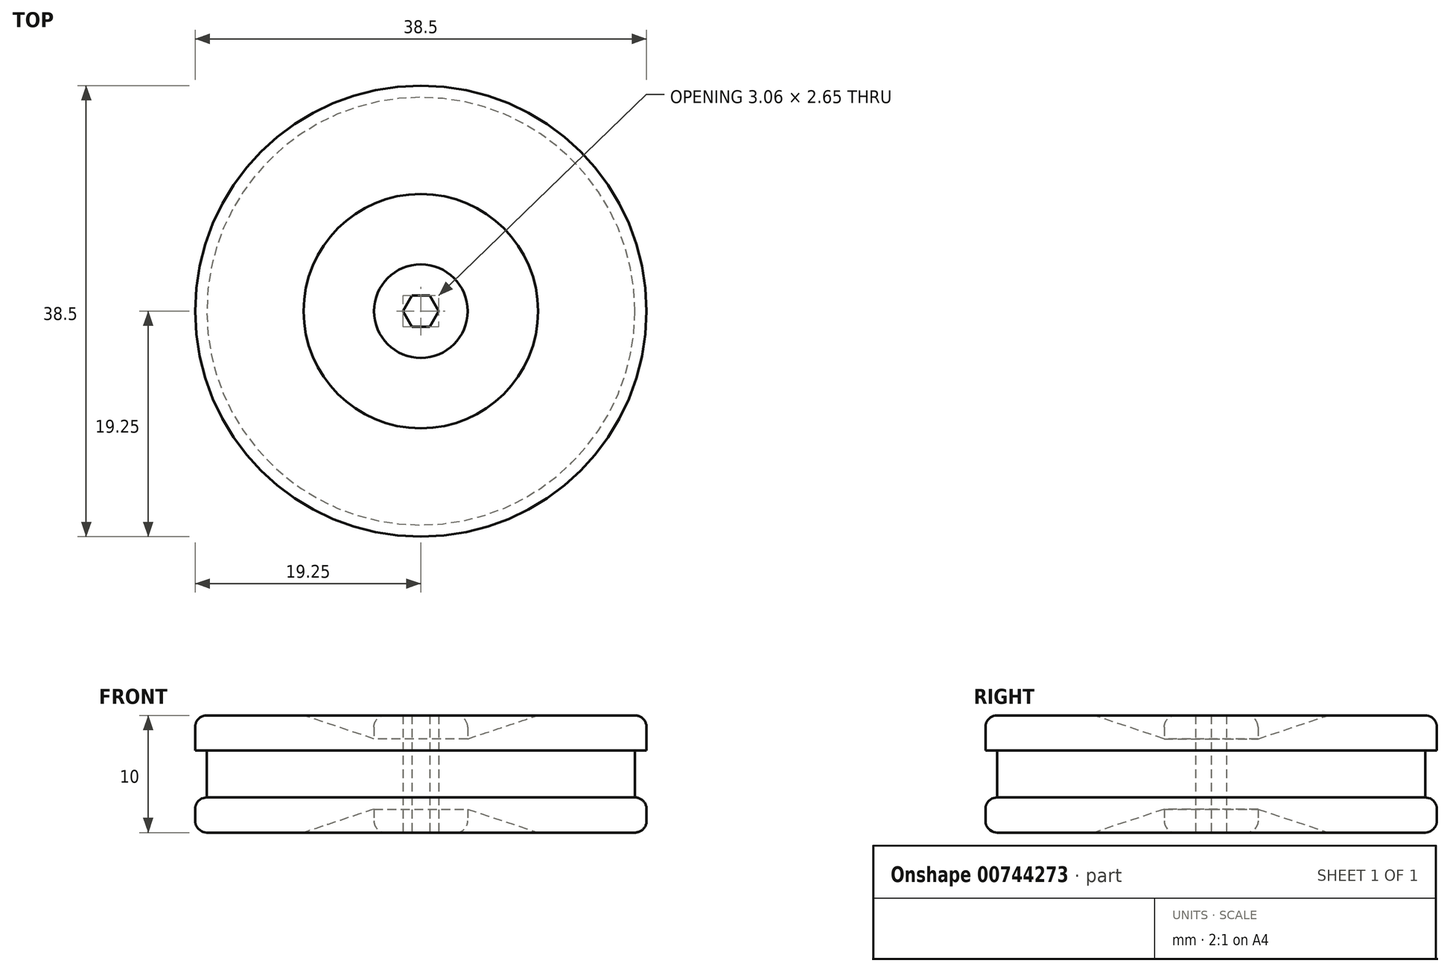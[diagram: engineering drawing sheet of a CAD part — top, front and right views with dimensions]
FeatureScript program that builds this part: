
annotation { "Feature Type Name" : "Feature", "Feature Type Description" : "" }
export const myFeature = defineFeature(function(context is Context, id is Id, definition is map)
    precondition{}
    {
        {
            var Q0;
            Q0=qCreatedBy(makeId("Top.planeOp"),FACE);
            var sketch = newSketch(context, id + "F0", { "sketchPlane" : qUnion([Q0])});
            skCircle(sketch, "E0", {"center": v(0, 0) * mm, "radius": 19.25 * mm});
            skCircle(sketch, "E1", {"center": v(0, 0) * mm, "radius": 1 * mm});
            skSolve(sketch);
        }
        {
            var Q0;
            Q0=qSketchRegion(id+"F0",true);
            extrude(context, id + "F1", {"entities" : qUnion([Q0]), "depth" : 10 * mm, "offsetDistance" : 25 * mm});
        }
        {
            var Q0;
            Q0=makeQuery(id+"F1.opExtrude","CAP_FACE",FACE,{"disambiguationData":[OSD([sQuery(id+"F0.wireOp",EDGE,"E0"),sQuery(id+"F0.wireOp",EDGE,"E1")])],"isStart":false});
            cPlane(context, id + "F2", {"entities" : qUnion([Q0]), "cplaneType" : CPlaneType.OFFSET, "offset" : 2 * mm, "oppositeDirection" : true, "width" : 150 * mm, "height" : 150 * mm});
        }
        {
            var Q0;
            Q0=qCreatedBy(id+"F2.planeOp",FACE);
            var sketch = newSketch(context, id + "F3", { "sketchPlane" : qUnion([Q0])});
            skCircle(sketch, "E2", {"center": v(0, 0) * mm, "radius": 4 * mm});
            skSolve(sketch);
        }
        {
            var Q0;
            Q0=makeQuery(id+"F1.opExtrude","CAP_FACE",FACE,{"disambiguationData":[OSD([sQuery(id+"F0.wireOp",EDGE,"E0"),sQuery(id+"F0.wireOp",EDGE,"E1")])],"isStart":false});
            var sketch = newSketch(context, id + "F4", { "sketchPlane" : qUnion([Q0])});
            skCircle(sketch, "E3", {"center": v(0, 0) * mm, "radius": 10 * mm});
            skSolve(sketch);
        }
        {
            var Q1;
            Q1=qSketchRegion(id+"F4",true);
            var Q2;
            Q2=qSketchRegion(id+"F3",true);
            loft(context, id + "F5", {"operationType" : NewBodyOperationType.REMOVE, "sheetProfilesArray" : [{ "sheetProfileEntities" : qUnion([Q1]) }, { "sheetProfileEntities" : qUnion([Q2]) }]});
        }
        {
            var Q0;
            Q0=makeQuery(id+"F0.imprint","IMPRINT",FACE,{"disambiguationData":[TD([[makeQuery(id+"F0.imprint","IMPRINT",EDGE,{"derivedFrom":sQuery(id+"F0.wireOp",EDGE,"E0")}),1.0]])]});
            cPlane(context, id + "F6", {"entities" : qUnion([Q0]), "cplaneType" : CPlaneType.OFFSET, "offset" : 2 * mm, "width" : 150 * mm, "height" : 150 * mm});
        }
        {
            var Q0;
            Q0=qCreatedBy(id+"F6.planeOp",FACE);
            var sketch = newSketch(context, id + "F7", { "sketchPlane" : qUnion([Q0])});
            skCircle(sketch, "E4", {"center": v(0, 0) * mm, "radius": 4 * mm});
            skSolve(sketch);
        }
        {
            var Q0;
            Q0=makeQuery(id+"F0.imprint","IMPRINT",FACE,{"disambiguationData":[TD([[makeQuery(id+"F0.imprint","IMPRINT",EDGE,{"derivedFrom":sQuery(id+"F0.wireOp",EDGE,"E0")}),1.0]])]});
            var sketch = newSketch(context, id + "F8", { "sketchPlane" : qUnion([Q0])});
            skCircle(sketch, "E5", {"center": v(0, 0) * mm, "radius": 10 * mm});
            skSolve(sketch);
        }
        {
            var Q1;
            Q1=qSketchRegion(id+"F8",true);
            var Q2;
            Q2=qSketchRegion(id+"F7",true);
            loft(context, id + "F9", {"operationType" : NewBodyOperationType.REMOVE, "sheetProfilesArray" : [{ "sheetProfileEntities" : qUnion([Q1]) }, { "sheetProfileEntities" : qUnion([Q2]) }]});
        }
        {
            var Q0;
            Q0=makeQuery(id+"F5.boolean.opBoolean","COPY",FACE,{"derivedFrom":makeQuery(id+"F5.opLoft","CAP_FACE",FACE,{"disambiguationData":[OSD([makeQuery(id+"F3.imprint","IMPRINT",FACE,{"disambiguationData":[TD([[makeQuery(id+"F3.imprint","IMPRINT",EDGE,{"derivedFrom":sQuery(id+"F3.wireOp",EDGE,"E2")}),1.0]])]})])],"isStart":true})});
            extrude(context, id + "F10", {"entities" : qUnion([Q0]), "operationType" : NewBodyOperationType.ADD, "depth" : 2 * mm, "offsetDistance" : 25 * mm});
        }
        {
            var Q0;
            Q0=makeQuery(id+"F0.imprint","IMPRINT",FACE,{"disambiguationData":[TD([[makeQuery(id+"F0.imprint","IMPRINT",EDGE,{"derivedFrom":sQuery(id+"F0.wireOp",EDGE,"E0")}),1.0]])]});
            var sketch = newSketch(context, id + "F11", { "sketchPlane" : qUnion([Q0])});
            skCircle(sketch, "E6", {"center": v(0, 0) * mm, "radius": 4 * mm});
            skCircle(sketch, "E7", {"center": v(0, 0) * mm, "radius": 1 * mm});
            skSolve(sketch);
        }
        {
            var Q0;
            Q0=qSketchRegion(id+"F11",true);
            extrude(context, id + "F12", {"entities" : qUnion([Q0]), "operationType" : NewBodyOperationType.ADD, "endBound" : BoundingType.UP_TO_NEXT, "depth" : 25 * mm, "offsetDistance" : 25 * mm});
        }
        {
            var Q0;
            Q0=qCreatedBy(makeId("Top.planeOp"),FACE);
            cPlane(context, id + "F13", {"entities" : qUnion([Q0]), "cplaneType" : CPlaneType.OFFSET, "offset" : 3 * mm, "width" : 150 * mm, "height" : 150 * mm});
        }
        {
            var Q0;
            Q0=qCreatedBy(id+"F13.planeOp",FACE);
            var sketch = newSketch(context, id + "F14", { "sketchPlane" : qUnion([Q0])});
            skCircle(sketch, "E8", {"center": v(0, 0) * mm, "radius": 19.25 * mm});
            skCircle(sketch, "E9", {"center": v(0, 0) * mm, "radius": 18.25 * mm});
            skSolve(sketch);
        }
        {
            var Q0;
            Q0=qSketchRegion(id+"F14",true);
            extrude(context, id + "F15", {"entities" : qUnion([Q0]), "operationType" : NewBodyOperationType.REMOVE, "depth" : 4 * mm, "offsetDistance" : 25 * mm});
        }
        {
            var Q0;
            Q0=makeQuery(id+"F10.opExtrude","CAP_EDGE",EDGE,{"disambiguationData":[OSD([sQuery(id+"F3.wireOp",EDGE,"E2")])],"isStart":false});
            var Q1;
            Q1=makeQuery(id+"F12.opExtrude","CAP_EDGE",EDGE,{"disambiguationData":[OSD([sQuery(id+"F11.wireOp",EDGE,"E6")])],"isStart":true});
            var Q2;
            Q2=makeQuery(id+"F1.opExtrude","CAP_EDGE",EDGE,{"disambiguationData":[OSD([sQuery(id+"F0.wireOp",EDGE,"E0")])],"isStart":false});
            var Q3;
            Q3=makeQuery(id+"F1.opExtrude","CAP_EDGE",EDGE,{"disambiguationData":[OSD([sQuery(id+"F0.wireOp",EDGE,"E0")])],"isStart":true});
            var Q4;
            Q4=makeQuery(id+"F15.boolean.opBoolean","COPY",EDGE,{"derivedFrom":makeQuery(id+"F15.opExtrude","CAP_EDGE",EDGE,{"disambiguationData":[OSD([sQuery(id+"F14.wireOp",EDGE,"E8")])],"isStart":false})});
            var Q5;
            Q5=makeQuery(id+"F15.boolean.opBoolean","COPY",EDGE,{"derivedFrom":makeQuery(id+"F15.opExtrude","CAP_EDGE",EDGE,{"disambiguationData":[OSD([sQuery(id+"F14.wireOp",EDGE,"E8")])],"isStart":true})});
            fillet(context, id + "F16", {"entities" : qUnion([Q0, Q1, Q2, Q3, Q4, Q5]), "radius" : 1 * mm, "tangentPropagation" : true, "allowEdgeOverflow" : false});
        }
        {
            var Q0;
            Q0=qCreatedBy(makeId("Top.planeOp"),FACE);
            var sketch = newSketch(context, id + "F17", { "sketchPlane" : qUnion([Q0])});
            skCircle(sketch, "E10.cCircle", {"center": v(0, 0) * mm, "radius": 1.33 * mm, "construction": true});
            skLineSegment(sketch, "E10.0", {"start": v(-0.76, 1.33) * mm, "end": v(0.76, 1.33) * mm});
            skLineSegment(sketch, "E10.1", {"start": v(0.76, 1.33) * mm, "end": v(1.53, 0) * mm});
            skLineSegment(sketch, "E10.2", {"start": v(1.53, 0) * mm, "end": v(0.76, -1.33) * mm});
            skLineSegment(sketch, "E10.3", {"start": v(0.76, -1.33) * mm, "end": v(-0.76, -1.33) * mm});
            skLineSegment(sketch, "E10.4", {"start": v(-0.76, -1.33) * mm, "end": v(-1.53, 0) * mm});
            skLineSegment(sketch, "E10.5", {"start": v(-1.53, 0) * mm, "end": v(-0.76, 1.33) * mm});
            skPoint(sketch, "E10.0.midPoint", {"position": v(0, 1.33) * mm});
            skSolve(sketch);
        }
        {
            var Q0;
            Q0 = qSketchRegion(id + "F17", true);
            extrude(context, id + "F18", {"entities" : qUnion([Q0]), "operationType" : NewBodyOperationType.REMOVE, "depth" : 25 * mm, "offsetDistance" : 25 * mm});
        }
    });
